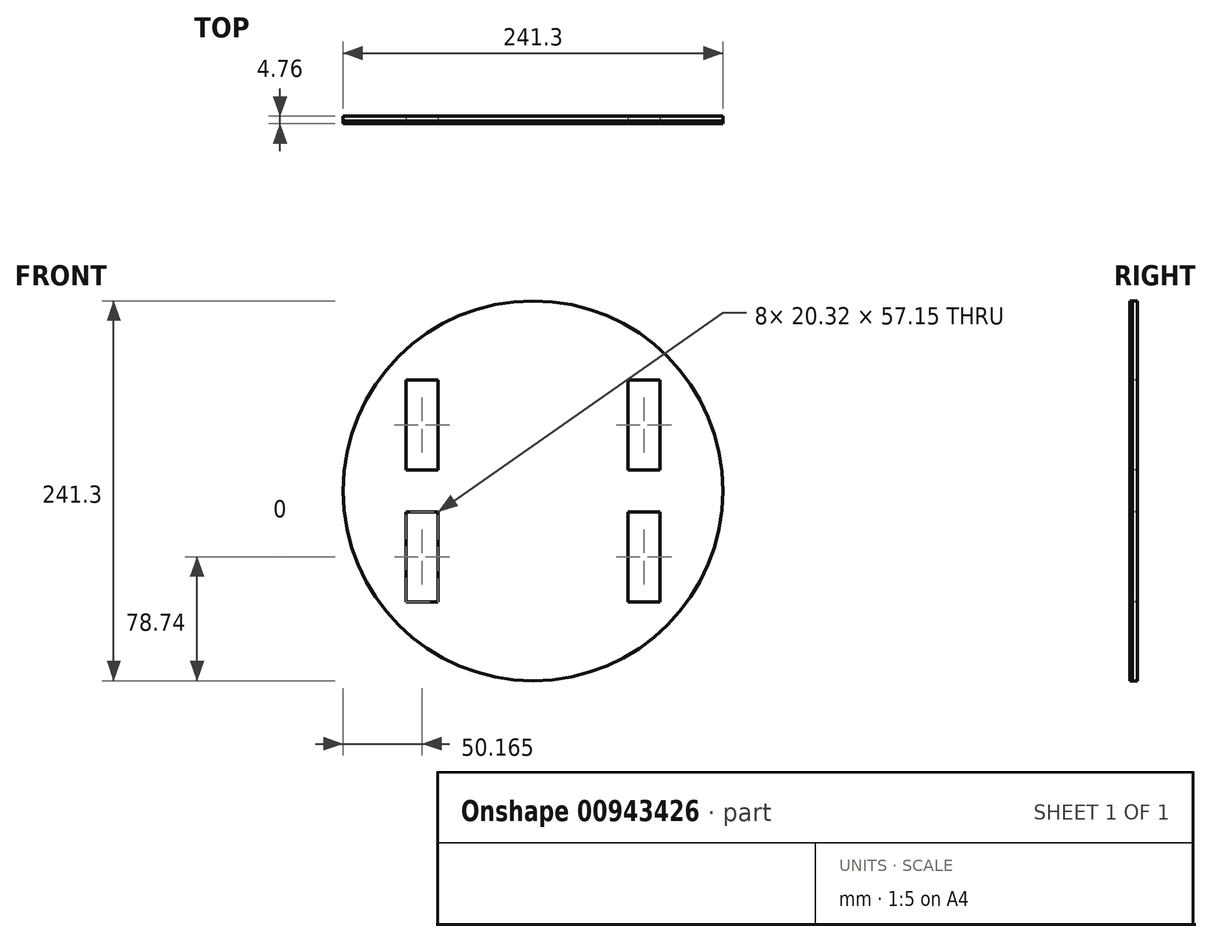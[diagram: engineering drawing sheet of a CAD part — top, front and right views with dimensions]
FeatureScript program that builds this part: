
annotation { "Feature Type Name" : "Feature", "Feature Type Description" : "" }
export const myFeature = defineFeature(function(context is Context, id is Id, definition is map)
    precondition{}
    {
        {
            var Q0;
            Q0=qCreatedBy(makeId("Front.planeOp"),FACE);
            var sketch = newSketch(context, id + "F0", { "sketchPlane" : qUnion([Q0])});
            skCircle(sketch, "E0", {"center": v(0, 0) * mm, "radius": 120.65 * mm});
            skSolve(sketch);
        }
        {
            var Q0;
            Q0=makeQuery(id+"F0.imprint","IMPRINT",FACE,{"disambiguationData":[TD([[makeQuery(id+"F0.imprint","IMPRINT",EDGE,{"derivedFrom":sQuery(id+"F0.wireOp",EDGE,"E0")}),1.0]])]});
            extrude(context, id + "F1", {"entities" : qUnion([Q0]), "depth" : 3.17 * mm, "offsetDistance" : 25.4 * mm});
        }
        {
            var Q0;
            Q0=makeQuery(id+"F1.opExtrude","CAP_FACE",FACE,{"disambiguationData":[OSD([sQuery(id+"F0.wireOp",EDGE,"E0")])],"isStart":false});
            var sketch = newSketch(context, id + "F2", { "sketchPlane" : qUnion([Q0])});
            skLineSegment(sketch, "E1", {"start": v(0, 120.65) * mm, "end": v(0, -120.65) * mm});
            skLineSegment(sketch, "E2", {"start": v(-60.32, -104.49) * mm, "end": v(-60.33, 104.49) * mm});
            skLineSegment(sketch, "E3", {"start": v(-80.64, -89.74) * mm, "end": v(-80.65, 89.74) * mm});
            skLineSegment(sketch, "E4.bottom", {"start": v(-60.33, 70.48) * mm, "end": v(-80.65, 70.48) * mm});
            skLineSegment(sketch, "E4.top", {"start": v(-60.33, 13.33) * mm, "end": v(-80.64, 13.33) * mm});
            skLineSegment(sketch, "E4.left", {"start": v(-60.33, 70.48) * mm, "end": v(-60.32, 13.33) * mm});
            skLineSegment(sketch, "E4.right", {"start": v(-80.65, 70.48) * mm, "end": v(-80.64, 13.33) * mm});
            skLineSegment(sketch, "E5.bottom", {"start": v(-80.64, -13.34) * mm, "end": v(-60.33, -13.34) * mm});
            skLineSegment(sketch, "E5.top", {"start": v(-80.64, -70.48) * mm, "end": v(-60.33, -70.48) * mm});
            skLineSegment(sketch, "E5.left", {"start": v(-80.64, -13.34) * mm, "end": v(-80.64, -70.48) * mm});
            skLineSegment(sketch, "E5.right", {"start": v(-60.32, -13.34) * mm, "end": v(-60.32, -70.48) * mm});
            skLineSegment(sketch, "E6", {"start": v(-70.48, 13.33) * mm, "end": v(-70.48, -13.34) * mm});
            skPoint(sketch, "E7", {"position": v(-70.48, 0) * mm});
            skLineSegment(sketch, "E8", {"start": v(-80.64, -41.91) * mm, "end": v(-60.32, -41.91) * mm});
            skLineSegment(sketch, "E9", {"start": v(-80.65, 41.9) * mm, "end": v(-60.32, 41.9) * mm});
            skLineSegment(sketch, "E10.MirrorCS", {"start": v(80.64, -70.48) * mm, "end": v(60.33, -70.48) * mm});
            skLineSegment(sketch, "E11.MirrorCS", {"start": v(60.33, 70.48) * mm, "end": v(80.65, 70.48) * mm});
            skLineSegment(sketch, "E12.MirrorCS", {"start": v(70.48, 13.33) * mm, "end": v(70.48, -13.34) * mm});
            skLineSegment(sketch, "E13.MirrorCS", {"start": v(80.64, -13.34) * mm, "end": v(80.64, -70.48) * mm});
            skLineSegment(sketch, "E14.MirrorCS", {"start": v(60.32, -13.34) * mm, "end": v(60.32, -70.48) * mm});
            skLineSegment(sketch, "E15.MirrorCS", {"start": v(80.65, 70.48) * mm, "end": v(80.64, 13.33) * mm});
            skLineSegment(sketch, "E16.MirrorCS", {"start": v(80.64, -13.34) * mm, "end": v(60.33, -13.34) * mm});
            skLineSegment(sketch, "E17.MirrorCS", {"start": v(60.33, 13.33) * mm, "end": v(80.64, 13.33) * mm});
            skLineSegment(sketch, "E18.MirrorCS", {"start": v(80.64, -41.91) * mm, "end": v(60.32, -41.91) * mm});
            skLineSegment(sketch, "E19.MirrorCS", {"start": v(60.33, 70.48) * mm, "end": v(60.32, 13.33) * mm});
            skLineSegment(sketch, "E20.MirrorCS", {"start": v(80.64, -89.74) * mm, "end": v(80.65, 89.74) * mm});
            skLineSegment(sketch, "E21.MirrorCS", {"start": v(60.32, -104.49) * mm, "end": v(60.33, 104.49) * mm});
            skPoint(sketch, "E22.MirrorP", {"position": v(70.48, 0) * mm});
            skLineSegment(sketch, "E23.MirrorCS", {"start": v(80.65, 41.9) * mm, "end": v(60.32, 41.9) * mm});
            skSolve(sketch);
        }
        {
            var Q0;
            {var subQ3=sQuery(id+"F2.wireOp",EDGE,"E23.MirrorCS");Q0=makeQuery(id+"F2.imprint","IMPRINT",FACE,{"disambiguationData":[TD([[makeQuery(id+"F2.imprint","IMPRINT",EDGE,{"derivedFrom":subQ3}),1.0]])]});}
            var Q1;
            {var subQ0=sQuery(id+"F2.wireOp",EDGE,"E11.MirrorCS");Q1=makeQuery(id+"F2.imprint","IMPRINT",FACE,{"disambiguationData":[TD([[makeQuery(id+"F2.imprint","IMPRINT",EDGE,{"derivedFrom":subQ0}),-1.0]])]});}
            var Q2;
            {var subQ3=sQuery(id+"F2.wireOp",EDGE,"E18.MirrorCS");Q2=makeQuery(id+"F2.imprint","IMPRINT",FACE,{"disambiguationData":[TD([[makeQuery(id+"F2.imprint","IMPRINT",EDGE,{"derivedFrom":subQ3}),-1.0]])]});}
            var Q3;
            {var subQ0=sQuery(id+"F2.wireOp",EDGE,"E10.MirrorCS");Q3=makeQuery(id+"F2.imprint","IMPRINT",FACE,{"disambiguationData":[TD([[makeQuery(id+"F2.imprint","IMPRINT",EDGE,{"derivedFrom":subQ0}),-1.0]])]});}
            var Q4;
            {var subQ0=sQuery(id+"F2.wireOp",EDGE,"E5.top");Q4=makeQuery(id+"F2.imprint","IMPRINT",FACE,{"disambiguationData":[TD([[makeQuery(id+"F2.imprint","IMPRINT",EDGE,{"derivedFrom":subQ0}),1.0]])]});}
            var Q5;
            {var subQ3=sQuery(id+"F2.wireOp",EDGE,"E8");Q5=makeQuery(id+"F2.imprint","IMPRINT",FACE,{"disambiguationData":[TD([[makeQuery(id+"F2.imprint","IMPRINT",EDGE,{"derivedFrom":subQ3}),1.0]])]});}
            var Q6;
            {var subQ3=sQuery(id+"F2.wireOp",EDGE,"E9");Q6=makeQuery(id+"F2.imprint","IMPRINT",FACE,{"disambiguationData":[TD([[makeQuery(id+"F2.imprint","IMPRINT",EDGE,{"derivedFrom":subQ3}),-1.0]])]});}
            var Q7;
            {var subQ0=sQuery(id+"F2.wireOp",EDGE,"E4.bottom");Q7=makeQuery(id+"F2.imprint","IMPRINT",FACE,{"disambiguationData":[TD([[makeQuery(id+"F2.imprint","IMPRINT",EDGE,{"derivedFrom":subQ0}),1.0]])]});}
            extrude(context, id + "F3", {"entities" : qUnion([Q0, Q1, Q2, Q3, Q4, Q5, Q6, Q7]), "operationType" : NewBodyOperationType.REMOVE, "oppositeDirection" : true, "depth" : 25.4 * mm, "offsetDistance" : 25.4 * mm});
        }
        {
            var Q0;
            Q0=makeQuery(id+"F1.opExtrude","CAP_FACE",FACE,{"disambiguationData":[OSD([sQuery(id+"F0.wireOp",EDGE,"E0")])],"isStart":false});
            var sketch = newSketch(context, id + "F4", { "sketchPlane" : qUnion([Q0])});
            skCircle(sketch, "E24.0.0", {"center": v(0, 0) * mm, "radius": 120.65 * mm});
            skSolve(sketch);
        }
        {
            var Q0;
            Q0=makeQuery(id+"F4.imprint","IMPRINT",FACE,{"disambiguationData":[TD([[makeQuery(id+"F4.imprint","IMPRINT",EDGE,{"derivedFrom":sQuery(id+"F4.wireOp",EDGE,"E24.0.0")}),1.0]])]});
            extrude(context, id + "F5", {"entities" : qUnion([Q0]), "depth" : 1.59 * mm, "offsetDistance" : 25.4 * mm});
        }
    });
